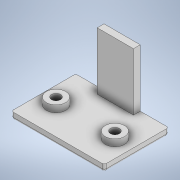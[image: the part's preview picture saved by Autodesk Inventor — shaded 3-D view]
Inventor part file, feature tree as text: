
AUTODESK INVENTOR PART (.ipt)
format: ipt  version: 2020 (Build 240168000, 168)  size: 189,952 bytes
history: native  units: in
note: dims shown in document units (in); Inventor stores cm internally (conversion verified against a paired STEP export)
features: extrude x8, sketch x8, fillet x1
ambient origin geometry x8: Origin, YZ Plane, XZ Plane, XY Plane, X Axis, Y Axis, Z Axis, Center Point
bodies: Solid1 (feature_tree)
feature tree (17):
  extrude  "Extrusion1"  Depth=1.6142in
  extrude  "Extrusion4"  Depth=0.1181in
  extrude  "Extrusion5"  Depth=0.1181in
  extrude  "Extrusion6"  Depth=0.1181in
  extrude  "Extrusion7"  Depth=0.1181in TaperAngle=0.0deg
  extrude  "Extrusion8"  Depth=0.1575in
  extrude  "Extrusion15"  Depth=0.2362in
  extrude  "Extrusion16"  Depth=0.1181in TaperAngle=0.0deg
  fillet  "Fillet3"  Radius=0.1575in
  sketch  "Sketch1"  dims[d0=1.6142in d1=1.2756in]
  sketch  "Sketch4"  dims[d2=0.1181in d3=0.0in d12=0.8465in]
  sketch  "Sketch5"  dims[d13=0.1181in d14=0.0in d15=0.8465in]
  sketch  "Sketch6"  dims[d16=0.1181in d17=0.0in d20=0.3346in]
  sketch  "Sketch7"  dims[d21=0.3346in d22=0.1181in d23=0.0in]
  sketch  "Sketch8"  dims[d24=0.1575in d25=0.1575in]
  sketch  "Sketch16"  dims[d26=0.2362in d27=0.0in d28=0.2362in]
  sketch  "Sketch17"  dims[d29=0.2362in d30=0.1181in d31=0.0in d56=0.1575in d57=1.9685in d58=0.0in d59=0.6299in d60=0.1181in d61=1.0in d62=0.0in d63=0.0394in d10=0.0197in d11=0.0344in]
